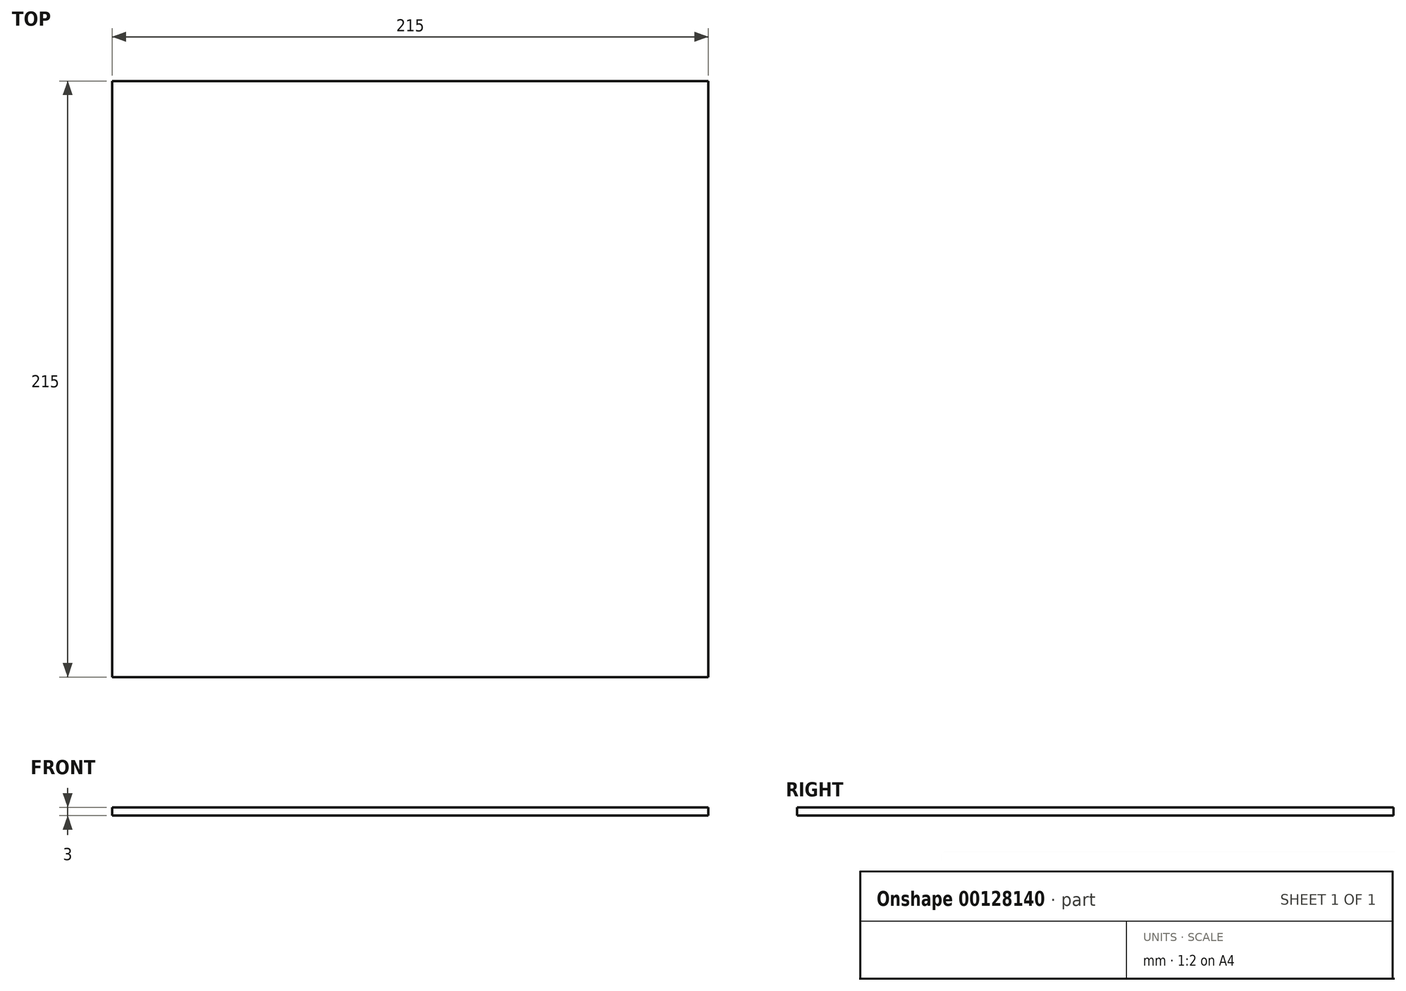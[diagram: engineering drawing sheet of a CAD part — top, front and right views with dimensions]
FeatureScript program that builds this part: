
annotation { "Feature Type Name" : "Feature", "Feature Type Description" : "" }
export const myFeature = defineFeature(function(context is Context, id is Id, definition is map)
    precondition{}
    {
        {
            var Q0;
            Q0=qCreatedBy(makeId("Top.planeOp"),FACE);
            var sketch = newSketch(context, id + "F0", { "sketchPlane" : qUnion([Q0])});
            skLineSegment(sketch, "E0.bottom", {"start": v(0, 0) * mm, "end": v(215, 0) * mm});
            skLineSegment(sketch, "E0.top", {"start": v(0, 215) * mm, "end": v(215, 215) * mm});
            skLineSegment(sketch, "E0.left", {"start": v(0, 0) * mm, "end": v(0, 215) * mm});
            skLineSegment(sketch, "E0.right", {"start": v(215, 0) * mm, "end": v(215, 215) * mm});
            skSolve(sketch);
        }
        {
            var Q0;
            Q0 = qSketchRegion(id + "F0", true);
            extrude(context, id + "F1", {"entities" : qUnion([Q0]), "depth" : 3 * mm});
        }
    });
